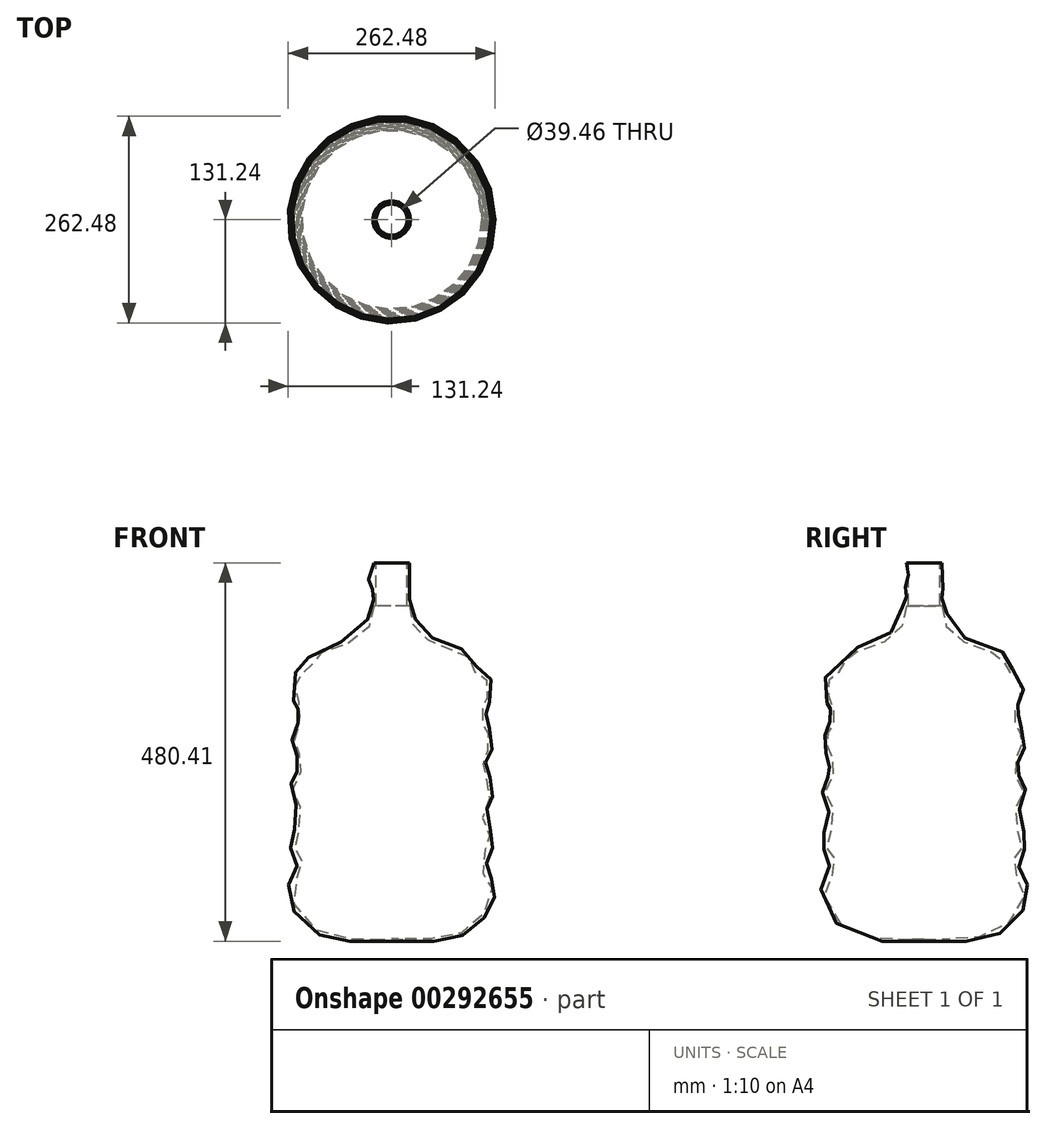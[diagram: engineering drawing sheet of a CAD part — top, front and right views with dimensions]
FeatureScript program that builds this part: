
annotation { "Feature Type Name" : "Feature", "Feature Type Description" : "" }
export const myFeature = defineFeature(function(context is Context, id is Id, definition is map)
    precondition{}
    {
        {
            var Q0;
            Q0=qCreatedBy(makeId("Front.planeOp"),FACE);
            var sketch = newSketch(context, id + "F0", { "sketchPlane" : qUnion([Q0])});
            skFitSpline(sketch, "E0", {"points": [v(22.44, 480) * mm, v(22.8, 471.3) * mm, v(22.2, 470.52) * mm, v(22.1, 457.75) * mm, v(23.15, 455.75) * mm, v(23.7, 442.3) * mm, v(23.14, 441.06) * mm, v(23.62, 430.8) * mm, v(26.33, 429.58) * mm, v(29.16, 412.95) * mm, v(36.59, 398.1) * mm, v(47.55, 387.14) * mm, v(68.06, 378.3) * mm, v(91.49, 370.16) * mm, v(104.93, 361.67) * mm, v(108.11, 347.88) * mm, v(117.66, 344.34) * mm, v(125.09, 335.85) * mm, v(126.15, 320.64) * mm, v(125.44, 307.91) * mm, v(123.03, 301.68) * mm, v(118.82, 299.15) * mm, v(119.26, 294.63) * mm, v(119.8, 288.97) * mm, v(119.44, 278.54) * mm, v(119.44, 272.53) * mm, v(123.68, 270.05) * mm, v(125.27, 265.1) * mm, v(126.6, 255.66) * mm, v(126.78, 240.81) * mm, v(123.24, 237.4) * mm, v(120.09, 235.09) * mm, v(119.03, 227.3) * mm, v(120.5, 218.48) * mm, v(120.52, 209.46) * mm, v(124.69, 207.38) * mm, v(127.36, 200.83) * mm, v(129.1, 188.97) * mm, v(127.67, 180.78) * mm, v(125.74, 176.91) * mm, v(121.73, 173.64) * mm, v(121.13, 168.6) * mm, v(121.13, 148.98) * mm, v(123.27, 141.91) * mm, v(127.88, 136.56) * mm, v(128.88, 129.62) * mm, v(129.3, 121.27) * mm, v(125.5, 114.73) * mm, v(121.6, 113.24) * mm, v(120.36, 101.35) * mm, v(120.15, 91.47) * mm, v(121.58, 84.33) * mm, v(126.63, 79.07) * mm, v(130, 75.28) * mm, v(131.21, 63.28) * mm, v(130, 52.15) * mm, v(126, 40.43) * mm, v(116.5, 27.93) * mm, v(102.99, 14.42) * mm, v(84.48, 4.42) * mm, v(65, 0) * mm, v(32.22, 0) * mm, v(0, 0) * mm], "startDerivative": vector(137.6, -840.54) * mm, "endDerivative": vector(-1094.97, -11.68) * mm});
            skLineSegment(sketch, "E1", {"start": v(22.44, 480) * mm, "end": v(20.15, 480) * mm});
            skLineSegment(sketch, "E2", {"start": v(19.73, 479.58) * mm, "end": v(19.73, 426.17) * mm});
            skLineSegment(sketch, "E3", {"start": v(20.15, 425.76) * mm, "end": v(22.05, 425.76) * mm});
            skFitSpline(sketch, "E4", {"points": [v(22.44, 425.76) * mm, v(24.57, 409.25) * mm, v(32.57, 393.24) * mm, v(52.58, 379) * mm, v(85.53, 366.8) * mm, v(97.55, 361.67) * mm, v(101.62, 351.06) * mm, v(104.56, 342.7) * mm, v(112.55, 339.97) * mm, v(121.38, 330.08) * mm, v(122.22, 313.68) * mm, v(118.23, 303.17) * mm, v(115.34, 300.3) * mm, v(115.56, 294.21) * mm, v(116.75, 283.43) * mm, v(115.83, 271.13) * mm, v(120.25, 268.3) * mm, v(122.73, 259.46) * mm, v(123.26, 243.2) * mm, v(117.6, 237) * mm, v(116.18, 226.75) * mm, v(116.33, 208.77) * mm, v(122.13, 202.82) * mm, v(125.1, 182.3) * mm, v(118.4, 175.9) * mm, v(117.97, 142.41) * mm, v(124.02, 134.85) * mm, v(123.84, 118.4) * mm, v(117.3, 114.73) * mm, v(116.2, 84.33) * mm, v(124.53, 73.99) * mm, v(126.68, 53.76) * mm, v(101.18, 17.76) * mm, v(66.47, 4.16) * mm, v(0, 2.24) * mm], "startDerivative": vector(36.2, -548.03) * mm, "endDerivative": vector(-1192.73, 15.05) * mm});
            skLineSegment(sketch, "E5", {"start": v(0, 2.24) * mm, "end": v(0, 0) * mm});
            skPoint(sketch, "E6.visualSharp", {"position": v(19.73, 480) * mm});
            skArc(sketch, "E6.filletArc", {"start": v(20.15, 480) * mm, "mid": v(19.85, 479.88) * mm, "end": v(19.73, 479.58) * mm});
            skPoint(sketch, "E7.visualSharp", {"position": v(19.73, 425.76) * mm});
            skArc(sketch, "E7.filletArc", {"start": v(19.73, 426.17) * mm, "mid": v(19.85, 425.88) * mm, "end": v(20.15, 425.76) * mm});
            skArc(sketch, "E8.filletArc", {"start": v(22.47, 425.37) * mm, "mid": v(22.33, 425.65) * mm, "end": v(22.05, 425.76) * mm});
            skSolve(sketch);
        }
        {
            var Q0;
            Q0 = qSketchRegion(id + "F0", true);
            var Q1;
            Q1=sQuery(id+"F0.wireOp",EDGE,"E5");
            revolve(context, id + "F1", {"entities" : qUnion([Q0]), "axis" : qUnion([Q1]), "revolveType" : RevolveType.FULL});
        }
    });
